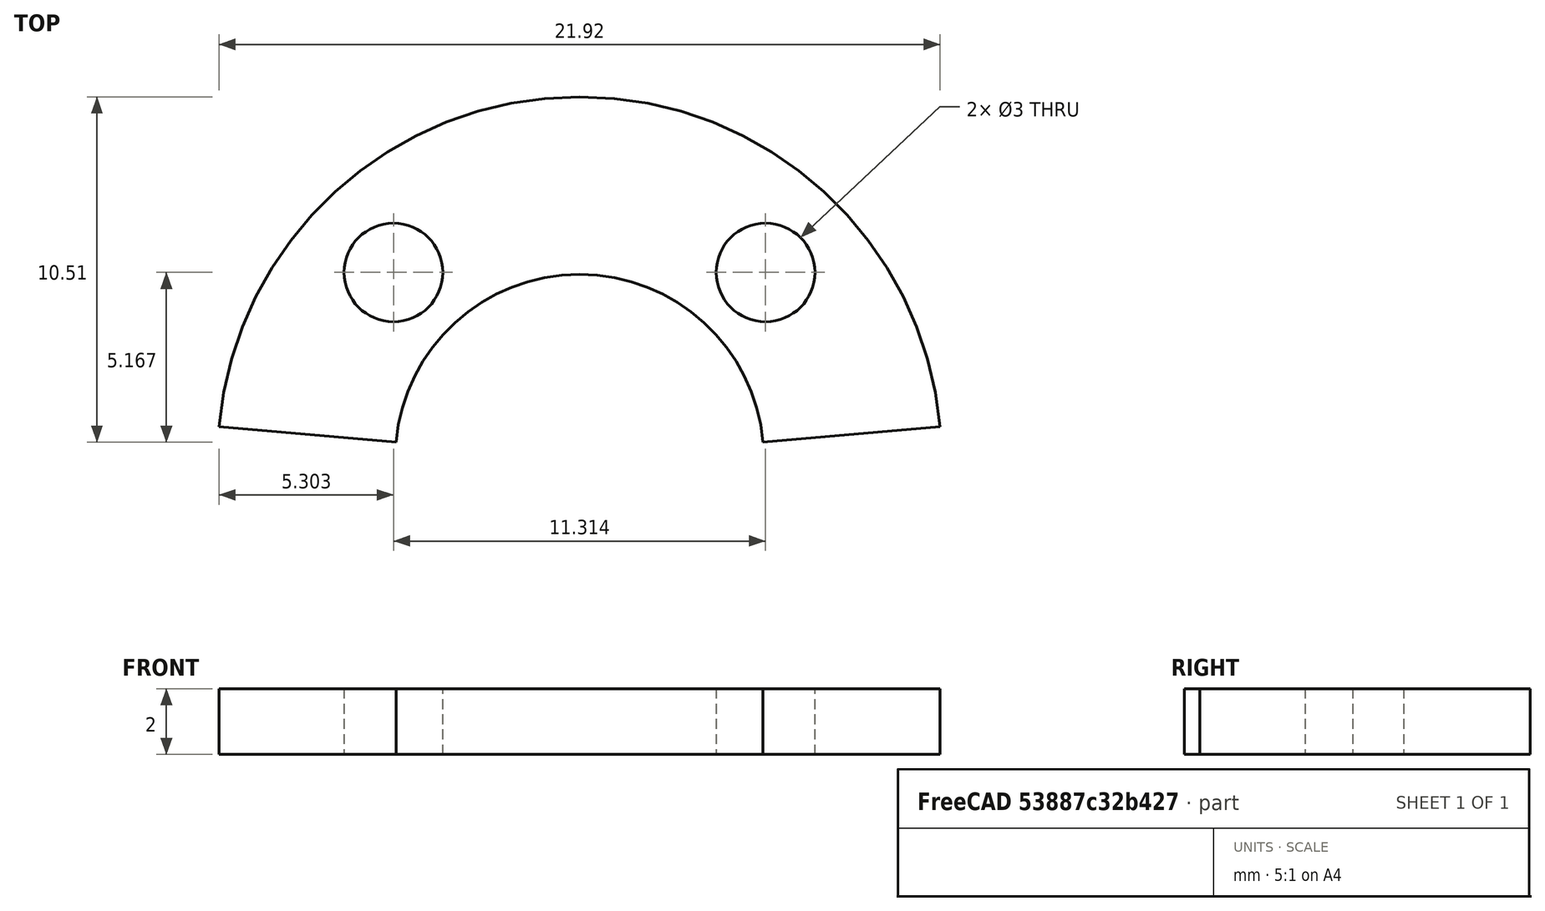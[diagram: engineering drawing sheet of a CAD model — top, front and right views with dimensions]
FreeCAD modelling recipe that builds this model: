
FCSTD DOCUMENT  (FreeCAD 0.19R)
Label: demi-rondelle_serrage_caoutchouc
License: All rights reserved
LicenseURL: http://en.wikipedia.org/wiki/All_rights_reserved
objects: Sketcher::SketchObject×1, PartDesign::Pad×1, PartDesign::Body×1
note: 4 computed .brp shape members not serialized (recipe doc carries the construction recipe); baked Part::Feature solids carry a one-line shape summary decoded from their .brp

FEATURE [Sketcher::SketchObject] Sketch
  FullyConstrained = true
  MapMode = 5
  Support = -> [XY_Plane]
  sketch-geometry (8):
    g0: ArcOfCircle CenterX=0 CenterY=0 CenterZ=0 NormalX=0 NormalY=0 NormalZ=1 AngleXU=0 Radius=11 StartAngle=0.0872665 EndAngle=3.05433
    g1: ArcOfCircle CenterX=0 CenterY=0 CenterZ=0 NormalX=0 NormalY=0 NormalZ=1 AngleXU=0 Radius=5.6 StartAngle=0.0872665 EndAngle=3.05433
    g2: LineSegment StartX=-5.57869 StartY=0.488072 StartZ=0 EndX=-10.9581 EndY=0.958713 EndZ=0
    g3: LineSegment StartX=5.57869 StartY=0.488072 StartZ=0 EndX=10.9581 EndY=0.958713 EndZ=0
    g4: Circle CenterX=-5.65685 CenterY=5.65685 CenterZ=0 NormalX=0 NormalY=0 NormalZ=1 AngleXU=0 Radius=1.5
    g5: Circle CenterX=5.65685 CenterY=5.65685 CenterZ=0 NormalX=0 NormalY=0 NormalZ=1 AngleXU=0 Radius=1.5
    g6: LineSegment StartX=0 StartY=0 StartZ=0 EndX=5.65685 EndY=5.65685 EndZ=0
    g7: LineSegment StartX=0 StartY=0 StartZ=0 EndX=-5.65685 EndY=5.65685 EndZ=0
  constraints (22):
    c: Coincident(g0,g-1)
    c: Coincident(g1,g0)
    c: Radius(g1) = 5.6
    c: Radius(g0) = 11
    c: Coincident(g2,g1)
    c: Coincident(g2,g0)
    c: Coincident(g3,g1)
    c: Coincident(g3,g0)
    c: PointOnObject(g0,g3)
    c: PointOnObject(g0,g2)
    c: Angle(g-1,g3) = 0.0872665
    c: Angle(g-1,g2) = 3.05433
    c: Radius(g5) = 1.5
    c: Radius(g4) = 1.5
    c: Coincident(g6,g0)
    c: Coincident(g6,g5)
    c: Coincident(g7,g0)
    c: Coincident(g7,g4)
    c: Angle(g-1,g6) = 0.785398
    c: Perpendicular(g6,g7)
    c: Distance(g7) = 8
    c: Distance(g6) = 8
FEATURE [PartDesign::Pad] Pad
  Direction = (1,1,1)
  Length = 2
  Length2 = 100
  Profile = -> Sketch
  Type = 0
FEATURE [PartDesign::Body] Body
  Group = -> [Sketch,Pad]
  Origin = -> Origin
  Tip = -> Pad
